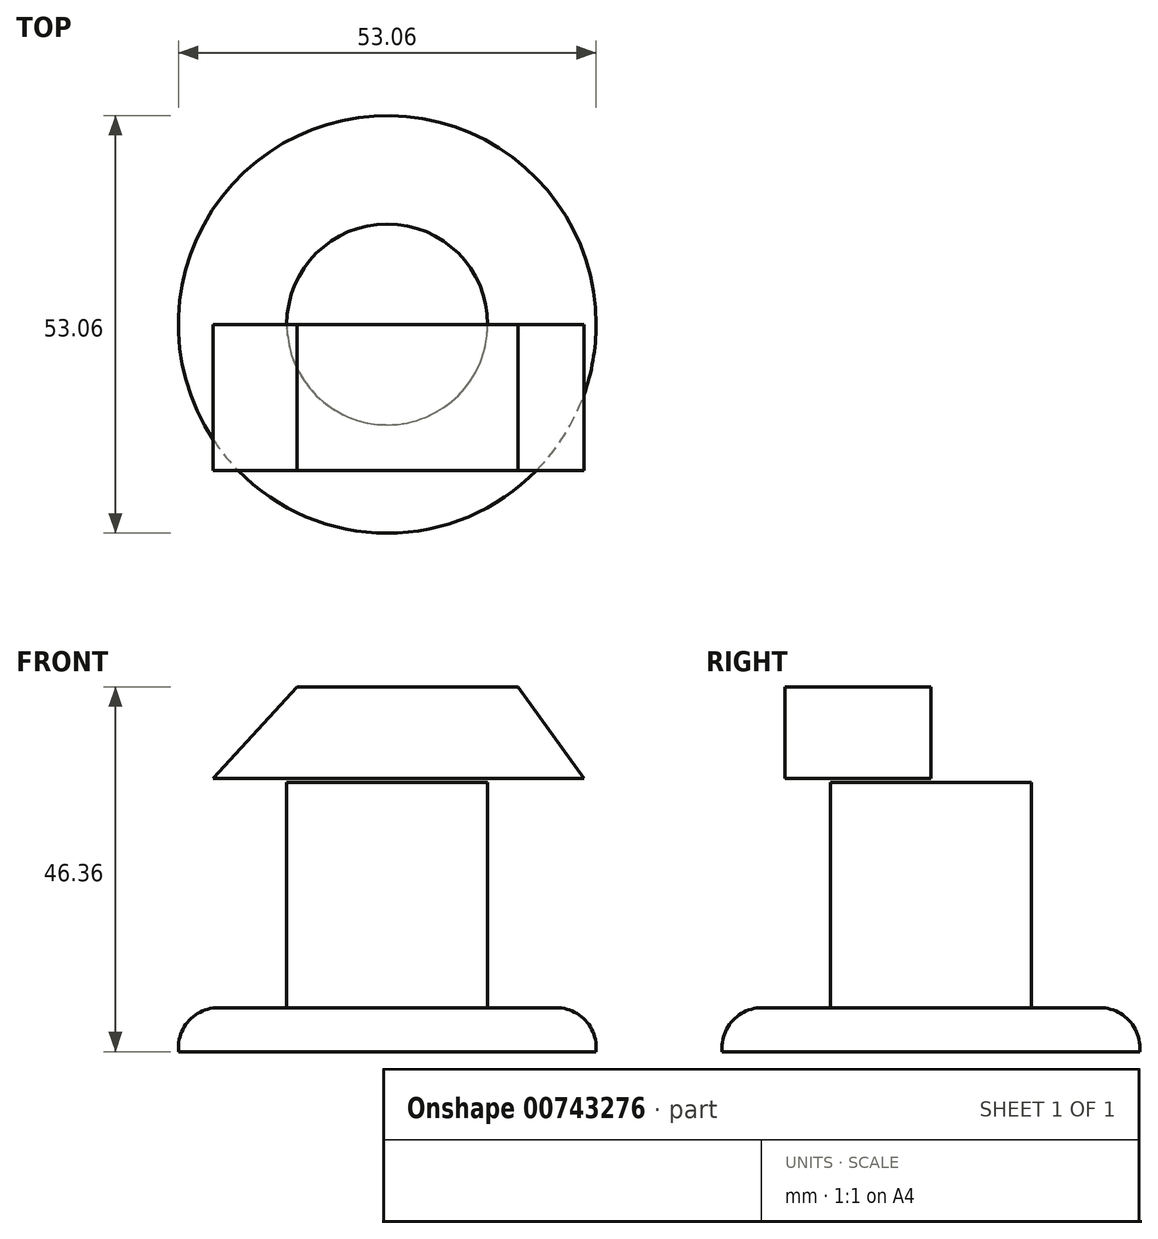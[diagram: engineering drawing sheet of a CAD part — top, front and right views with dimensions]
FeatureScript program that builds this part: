
annotation { "Feature Type Name" : "Feature", "Feature Type Description" : "" }
export const myFeature = defineFeature(function(context is Context, id is Id, definition is map)
    precondition{}
    {
        {
            var Q0;
            Q0=qCreatedBy(makeId("Top.planeOp"),FACE);
            var sketch = newSketch(context, id + "F0", { "sketchPlane" : qUnion([Q0])});
            skCircle(sketch, "E0", {"center": v(0, 0) * mm, "radius": 26.53 * mm});
            skSolve(sketch);
        }
        {
            var Q0;
            Q0 = qSketchRegion(id + "F0", true);
            extrude(context, id + "F1", {"entities" : qUnion([Q0]), "depth" : 5.6 * mm, "offsetDistance" : 25.4 * mm});
        }
        {
            var Q0;
            Q0=qCreatedBy(makeId("Top.planeOp"),FACE);
            var sketch = newSketch(context, id + "F2", { "sketchPlane" : qUnion([Q0])});
            skCircle(sketch, "E1", {"center": v(0, 0) * mm, "radius": 12.76 * mm});
            skSolve(sketch);
        }
        {
            var Q0;
            Q0 = qSketchRegion(id + "F2", true);
            extrude(context, id + "F3", {"entities" : qUnion([Q0]), "operationType" : NewBodyOperationType.ADD, "depth" : 34.23 * mm, "offsetDistance" : 25.4 * mm});
        }
        {
            var Q0;
            Q0=qCreatedBy(makeId("Front.planeOp"),FACE);
            var sketch = newSketch(context, id + "F4", { "sketchPlane" : qUnion([Q0])});
            skLineSegment(sketch, "E2", {"start": v(0, 34.74) * mm, "end": v(-22.13, 34.74) * mm});
            skLineSegment(sketch, "E3", {"start": v(-22.13, 34.74) * mm, "end": v(24.96, 34.74) * mm});
            skLineSegment(sketch, "E4", {"start": v(-22.13, 34.74) * mm, "end": v(-11.43, 46.36) * mm});
            skLineSegment(sketch, "E5", {"start": v(-11.43, 46.36) * mm, "end": v(16.62, 46.36) * mm});
            skLineSegment(sketch, "E6", {"start": v(16.62, 46.36) * mm, "end": v(24.96, 34.74) * mm});
            skSolve(sketch);
        }
        {
            var Q0;
            {var subQ0=sQuery(id+"F4.wireOp",EDGE,"E4");Q0=makeQuery(id+"F4.imprint","IMPRINT",FACE,{"disambiguationData":[TD([[makeQuery(id+"F4.imprint","IMPRINT",EDGE,{"derivedFrom":subQ0}),-1.0]])]});}
            extrude(context, id + "F5", {"entities" : qUnion([Q0]), "depth" : 18.54 * mm, "offsetDistance" : 25.4 * mm});
        }
        {
            var Q0;
            Q0=makeQuery(id+"F1.opExtrude","CAP_EDGE",EDGE,{"disambiguationData":[OSD([sQuery(id+"F0.wireOp",EDGE,"E0")])],"isStart":false});
            fillet(context, id + "F6", {"entities" : qUnion([Q0]), "radius" : 5.08 * mm, "tangentPropagation" : true, "allowEdgeOverflow" : false});
        }
    });
